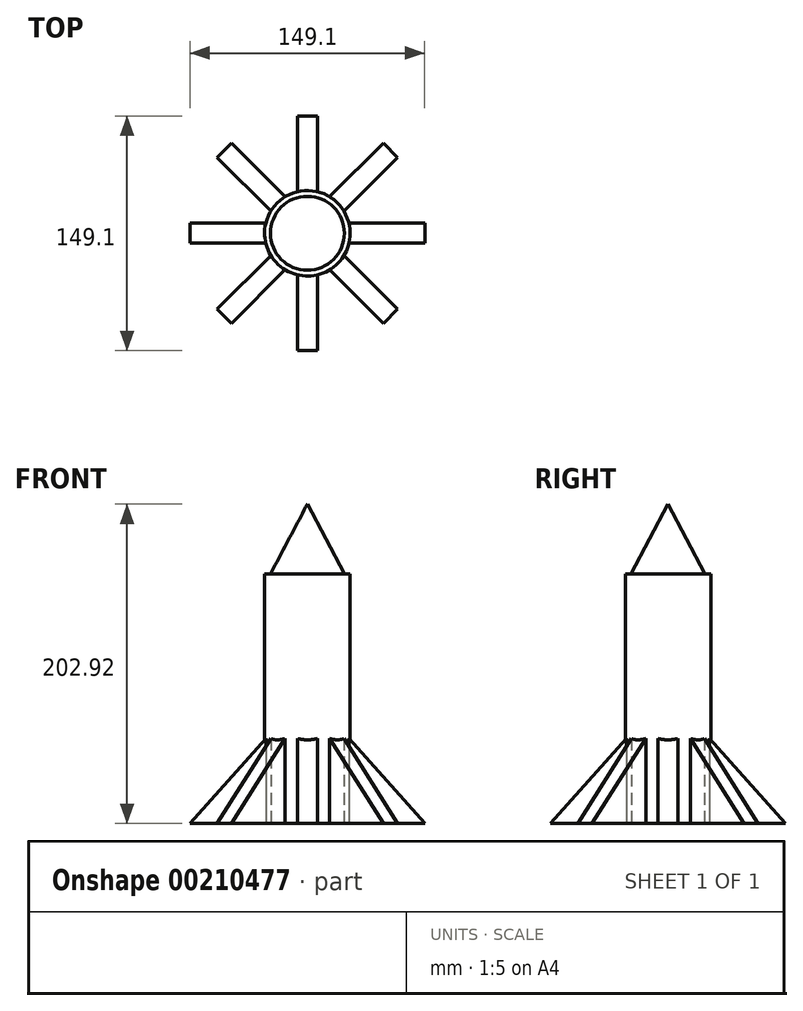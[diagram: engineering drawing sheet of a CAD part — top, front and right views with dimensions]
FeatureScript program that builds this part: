
annotation { "Feature Type Name" : "Feature", "Feature Type Description" : "" }
export const myFeature = defineFeature(function(context is Context, id is Id, definition is map)
    precondition{}
    {
        {
            var Q0;
            Q0=qCreatedBy(makeId("Top.planeOp"),FACE);
            var sketch = newSketch(context, id + "F0", { "sketchPlane" : qUnion([Q0])});
            skCircle(sketch, "E0", {"center": v(0, 0) * mm, "radius": 27.15 * mm});
            skSolve(sketch);
        }
        {
            var Q0;
            Q0 = qSketchRegion(id + "F0", true);
            extrude(context, id + "F1", {"entities" : qUnion([Q0]), "depth" : 158.5 * mm});
        }
        {
            var Q0;
            Q0=qCreatedBy(makeId("Right.planeOp"),FACE);
            var sketch = newSketch(context, id + "F2", { "sketchPlane" : qUnion([Q0])});
            skLineSegment(sketch, "E1", {"start": v(6.66, 0) * mm, "end": v(6.66, 76.2) * mm});
            skLineSegment(sketch, "E2", {"start": v(6.66, 76.2) * mm, "end": v(74.55, 0) * mm});
            skLineSegment(sketch, "E3", {"start": v(74.55, 0) * mm, "end": v(6.66, 0) * mm});
            skSolve(sketch);
        }
        {
            var Q0;
            Q0 = qSketchRegion(id + "F2", true);
            extrude(context, id + "F3", {"entities" : qUnion([Q0]), "operationType" : NewBodyOperationType.ADD, "endBound" : BoundingType.SYMMETRIC, "depth" : 12.7 * mm});
        }
        {
            var Q0;
            Q0=makeQuery(id+"F1.opExtrude","SWEPT_BODY",BODY,{"disambiguationData":[OSD([sQuery(id+"F0.wireOp",EDGE,"E0")])]});
            var Q1;
            Q1=makeQuery(id+"F1.opExtrude","SWEPT_FACE",FACE,{"disambiguationData":[OSD([sQuery(id+"F0.wireOp",EDGE,"E0")])]});
            circularPattern(context, id + "F4", {"entities" : qUnion([Q0]), "axis" : qUnion([Q1]), "angle" : 360 * degree, "instanceCount" : 8, "equalSpace" : true});
        }
        {
            var Q0;
            Q0=qCreatedBy(makeId("Right.planeOp"),FACE);
            var sketch = newSketch(context, id + "F5", { "sketchPlane" : qUnion([Q0])});
            skLineSegment(sketch, "E4", {"start": v(0, 154.48) * mm, "end": v(0, 202.92) * mm});
            skLineSegment(sketch, "E5", {"start": v(0, 202.92) * mm, "end": v(-25.59, 154.48) * mm});
            skLineSegment(sketch, "E6", {"start": v(-25.59, 154.48) * mm, "end": v(0, 154.48) * mm});
            skSolve(sketch);
        }
        {
            var Q0;
            Q0 = qSketchRegion(id + "F5", true);
            var Q1;
            Q1=sQuery(id+"F5.wireOp",EDGE,"E4");
            revolve(context, id + "F6", {"operationType" : NewBodyOperationType.ADD, "entities" : qUnion([Q0]), "axis" : qUnion([Q1]), "revolveType" : RevolveType.FULL});
        }
    });
